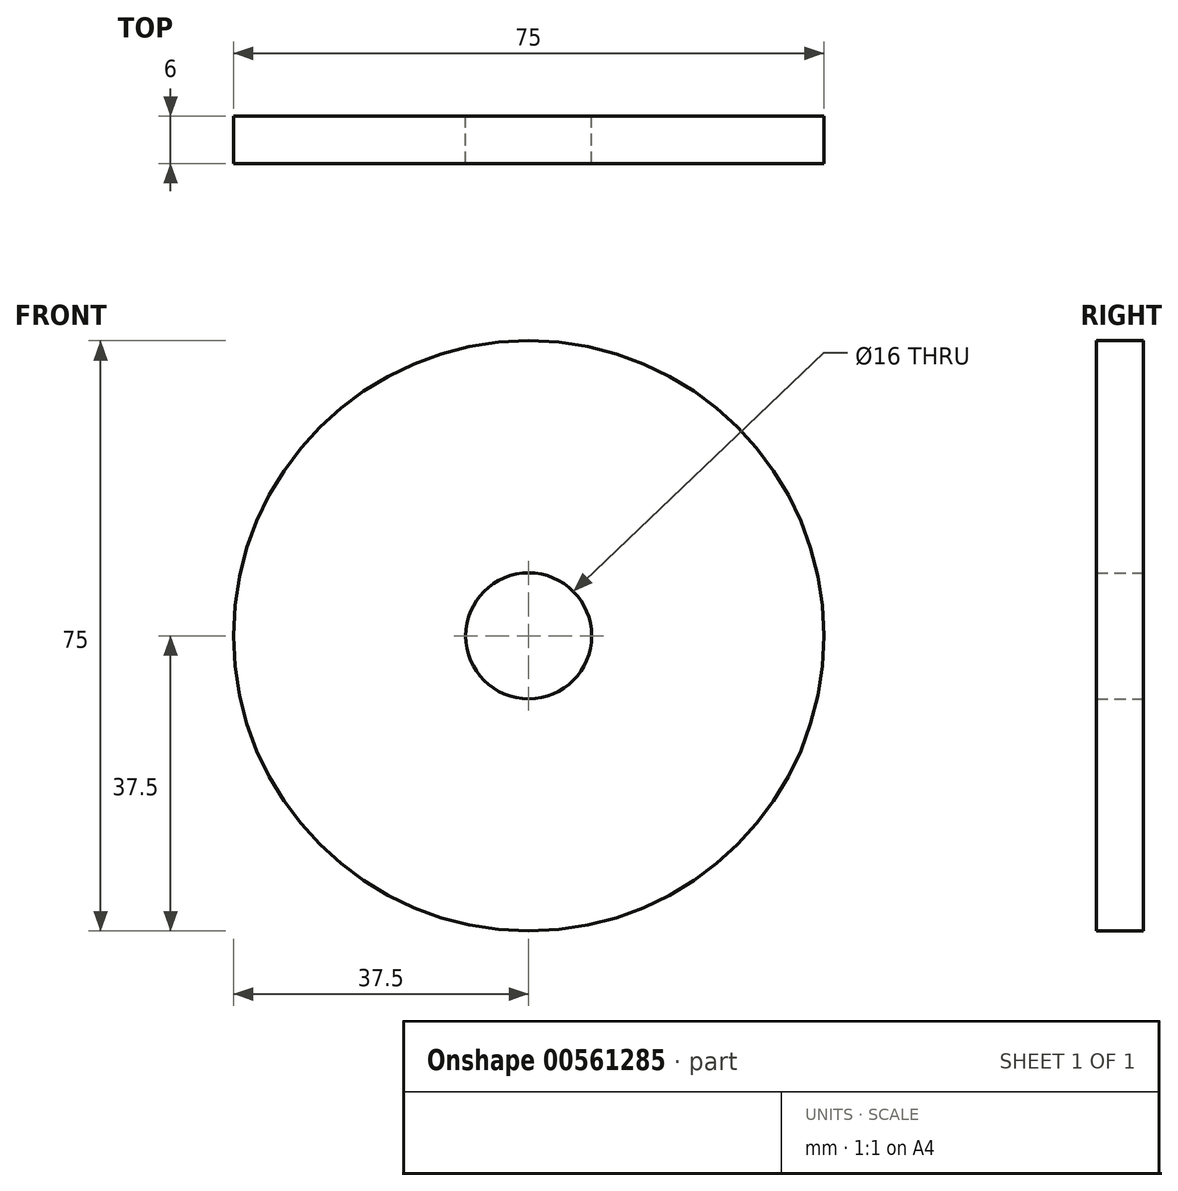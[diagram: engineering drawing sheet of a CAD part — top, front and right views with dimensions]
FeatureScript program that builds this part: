
annotation { "Feature Type Name" : "Feature", "Feature Type Description" : "" }
export const myFeature = defineFeature(function(context is Context, id is Id, definition is map)
    precondition{}
    {
        {
            var Q0;
            Q0=qCreatedBy(makeId("Front.planeOp"),FACE);
            var sketch = newSketch(context, id + "F0", { "sketchPlane" : qUnion([Q0])});
            skCircle(sketch, "E0", {"center": v(0, 0) * mm, "radius": 37.5 * mm});
            skCircle(sketch, "E1", {"center": v(0, 0) * mm, "radius": 8 * mm});
            skSolve(sketch);
        }
        {
            var Q0;
            Q0 = qSketchRegion(id + "F0", true);
            extrude(context, id + "F1", {"entities" : qUnion([Q0]), "depth" : 6 * mm, "offsetDistance" : 25 * mm});
        }
    });
